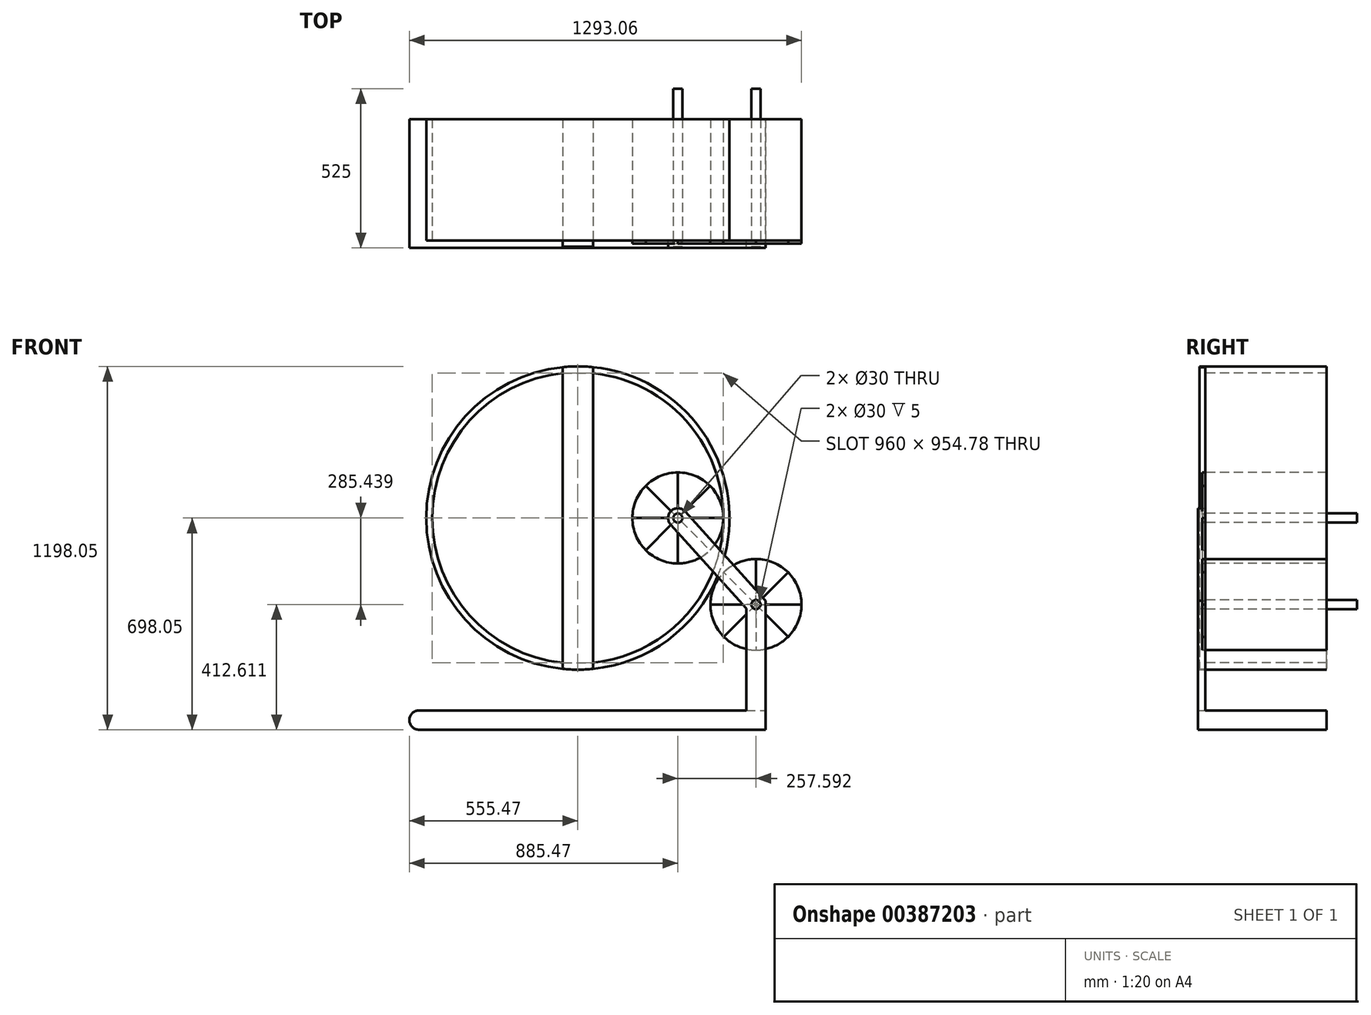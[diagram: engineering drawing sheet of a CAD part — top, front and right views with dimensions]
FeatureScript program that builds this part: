
annotation { "Feature Type Name" : "Feature", "Feature Type Description" : "" }
export const myFeature = defineFeature(function(context is Context, id is Id, definition is map)
    precondition{}
    {
        {
            var Q0;
            Q0=qCreatedBy(makeId("Front.planeOp"),FACE);
            var sketch = newSketch(context, id + "F0", { "sketchPlane" : qUnion([Q0])});
            skCircle(sketch, "E0", {"center": v(0, 0) * mm, "radius": 500 * mm});
            skArc(sketch, "E1", {"start": v(50, -477.39) * mm, "mid": v(480, 0) * mm, "end": v(50, 477.39) * mm});
            skCircle(sketch, "E2", {"center": v(330, 0) * mm, "radius": 150 * mm});
            skCircle(sketch, "E3", {"center": v(587.6, -285.44) * mm, "radius": 150 * mm});
            skLineSegment(sketch, "E4", {"start": v(330, 0) * mm, "end": v(587.6, -285.44) * mm});
            skLineSegment(sketch, "E5", {"start": v(587.6, -666.05) * mm, "end": v(-523.47, -666.05) * mm});
            skLineSegment(sketch, "E6", {"start": v(587.6, -666.05) * mm, "end": v(587.6, -285.44) * mm});
            skLineSegment(sketch, "E7.0", {"start": v(555.6, -634.05) * mm, "end": v(-523.47, -634.05) * mm});
            skLineSegment(sketch, "E7.1", {"start": v(555.6, -634.05) * mm, "end": v(555.6, -297.74) * mm});
            skLineSegment(sketch, "E7.2", {"start": v(306.24, -21.44) * mm, "end": v(555.6, -297.74) * mm});
            skLineSegment(sketch, "E8.0", {"start": v(619.6, -698.05) * mm, "end": v(-523.47, -698.05) * mm});
            skLineSegment(sketch, "E8.1", {"start": v(619.6, -698.05) * mm, "end": v(619.6, -273.13) * mm});
            skLineSegment(sketch, "E8.2", {"start": v(353.76, 21.44) * mm, "end": v(619.6, -273.13) * mm});
            skArc(sketch, "E9", {"start": v(-523.47, -634.05) * mm, "mid": v(-555.47, -666.05) * mm, "end": v(-523.47, -698.05) * mm});
            skArc(sketch, "E10", {"start": v(353.76, 21.44) * mm, "mid": v(308.56, 23.76) * mm, "end": v(306.24, -21.44) * mm});
            skCircle(sketch, "E11", {"center": v(330, 0) * mm, "radius": 15 * mm});
            skCircle(sketch, "E12", {"center": v(587.6, -285.44) * mm, "radius": 15 * mm});
            skLineSegment(sketch, "E13.0", {"start": v(50, 0) * mm, "end": v(50, 477.39) * mm});
            skLineSegment(sketch, "E13.1", {"start": v(50, 0) * mm, "end": v(50, -477.39) * mm});
            skLineSegment(sketch, "E14.0", {"start": v(-50, 0) * mm, "end": v(-50, 477.39) * mm});
            skLineSegment(sketch, "E14.1", {"start": v(-50, 0) * mm, "end": v(-50, -477.39) * mm});
            skArc(sketch, "E15.trimOffspring", {"start": v(-50, 477.39) * mm, "mid": v(-480, 0) * mm, "end": v(-50, -477.39) * mm});
            skCircle(sketch, "E16.cCircle", {"center": v(587.6, -285.44) * mm, "radius": 24.02 * mm, "construction": true});
            skLineSegment(sketch, "E16.0", {"start": v(613.98, -293.98) * mm, "end": v(593.39, -312.56) * mm});
            skLineSegment(sketch, "E16.1", {"start": v(593.39, -312.56) * mm, "end": v(567, -304.02) * mm});
            skLineSegment(sketch, "E16.2", {"start": v(567, -304.02) * mm, "end": v(561.2, -276.9) * mm});
            skLineSegment(sketch, "E16.3", {"start": v(561.2, -276.9) * mm, "end": v(581.8, -258.32) * mm});
            skLineSegment(sketch, "E16.4", {"start": v(581.8, -258.32) * mm, "end": v(608.18, -266.86) * mm});
            skLineSegment(sketch, "E16.5", {"start": v(608.18, -266.86) * mm, "end": v(613.98, -293.98) * mm});
            skPoint(sketch, "E16.0.midPoint", {"position": v(603.68, -303.27) * mm});
            skCircle(sketch, "E17.cCircle", {"center": v(330, 0) * mm, "radius": 22.44 * mm, "construction": true});
            skLineSegment(sketch, "E17.0", {"start": v(350.26, -16.15) * mm, "end": v(326.14, -25.63) * mm});
            skLineSegment(sketch, "E17.1", {"start": v(326.14, -25.63) * mm, "end": v(305.88, -9.47) * mm});
            skLineSegment(sketch, "E17.2", {"start": v(305.88, -9.47) * mm, "end": v(309.74, 16.15) * mm});
            skLineSegment(sketch, "E17.3", {"start": v(309.74, 16.15) * mm, "end": v(333.86, 25.63) * mm});
            skLineSegment(sketch, "E17.4", {"start": v(333.86, 25.63) * mm, "end": v(354.12, 9.47) * mm});
            skLineSegment(sketch, "E17.5", {"start": v(354.12, 9.47) * mm, "end": v(350.26, -16.15) * mm});
            skPoint(sketch, "E17.0.midPoint", {"position": v(338.2, -20.9) * mm});
            skLineSegment(sketch, "E18", {"start": v(555.6, -634.05) * mm, "end": v(619.6, -634.05) * mm});
            skLineSegment(sketch, "E19", {"start": v(-50, 477.39) * mm, "end": v(-50, 497.5) * mm});
            skLineSegment(sketch, "E20", {"start": v(50, 477.39) * mm, "end": v(50, 497.5) * mm});
            skLineSegment(sketch, "E21", {"start": v(-50, 477.39) * mm, "end": v(50, 477.39) * mm});
            skLineSegment(sketch, "E22", {"start": v(-50, -477.39) * mm, "end": v(-50, -497.5) * mm});
            skLineSegment(sketch, "E23", {"start": v(-50, -477.39) * mm, "end": v(50, -477.39) * mm});
            skLineSegment(sketch, "E24", {"start": v(50, -477.39) * mm, "end": v(50, -497.5) * mm});
            skSolve(sketch);
        }
        {
            var Q0;
            {var subQ1=sQuery(id+"F0.wireOp",EDGE,"E7.0");Q0=makeQuery(id+"F0.imprint","IMPRINT",FACE,{"disambiguationData":[TD([[makeQuery(id+"F0.imprint","IMPRINT",EDGE,{"derivedFrom":subQ1}),1.0]])]});}
            var Q1;
            {var subQ10=sQuery(id+"F0.wireOp",EDGE,"E16.2");Q1=makeQuery(id+"F0.imprint","IMPRINT",FACE,{"disambiguationData":[TD([[makeQuery(id+"F0.imprint","IMPRINT",EDGE,{"derivedFrom":subQ10}),1.0]])]});}
            var Q2;
            {var subQ8=sQuery(id+"F0.wireOp",EDGE,"E16.0");Q2=makeQuery(id+"F0.imprint","IMPRINT",FACE,{"disambiguationData":[TD([[makeQuery(id+"F0.imprint","IMPRINT",EDGE,{"derivedFrom":subQ8}),1.0]])]});}
            var Q3;
            {var subQ0=sQuery(id+"F0.wireOp",EDGE,"E7.2");var subQ1=sQuery(id+"F0.wireOp",EDGE,"E0");var subQ2=makeQuery(id+"F0.imprint","INTERSECT",VERTEX,{"derivedFrom":[subQ1,subQ0]});Q3=makeQuery(id+"F0.imprint","IMPRINT",FACE,{"disambiguationData":[TD([[makeQuery(id+"F0.imprint","IMPRINT",EDGE,{"disambiguationData":[TD([[subQ2,-1.0]])],"derivedFrom":subQ1}),-1.0]])]});}
            var Q4;
            {var subQ0=sQuery(id+"F0.wireOp",EDGE,"E7.2");var subQ1=sQuery(id+"F0.wireOp",EDGE,"E0");var subQ2=makeQuery(id+"F0.imprint","INTERSECT",VERTEX,{"derivedFrom":[subQ1,subQ0]});Q4=makeQuery(id+"F0.imprint","IMPRINT",FACE,{"disambiguationData":[TD([[makeQuery(id+"F0.imprint","IMPRINT",EDGE,{"disambiguationData":[TD([[subQ2,-1.0]])],"derivedFrom":subQ1}),1.0]])]});}
            var Q5;
            {var subQ0=sQuery(id+"F0.wireOp",EDGE,"E7.2");var subQ1=sQuery(id+"F0.wireOp",EDGE,"E1");var subQ2=makeQuery(id+"F0.imprint","INTERSECT",VERTEX,{"derivedFrom":[subQ1,subQ0]});Q5=makeQuery(id+"F0.imprint","IMPRINT",FACE,{"disambiguationData":[TD([[makeQuery(id+"F0.imprint","IMPRINT",EDGE,{"disambiguationData":[TD([[subQ2,-1.0]])],"derivedFrom":subQ1}),1.0]])]});}
            var Q6;
            {var subQ0=sQuery(id+"F0.wireOp",EDGE,"E4");var subQ1=sQuery(id+"F0.wireOp",EDGE,"E1");var subQ2=makeQuery(id+"F0.imprint","INTERSECT",VERTEX,{"derivedFrom":[subQ1,subQ0]});Q6=makeQuery(id+"F0.imprint","IMPRINT",FACE,{"disambiguationData":[TD([[makeQuery(id+"F0.imprint","IMPRINT",EDGE,{"disambiguationData":[TD([[subQ2,-1.0]])],"derivedFrom":subQ1}),1.0]])]});}
            var Q7;
            {var subQ4=sQuery(id+"F0.wireOp",EDGE,"E10");Q7=makeQuery(id+"F0.imprint","IMPRINT",FACE,{"disambiguationData":[TD([[makeQuery(id+"F0.imprint","IMPRINT",EDGE,{"derivedFrom":subQ4}),1.0]])]});}
            var Q8;
            {var subQ0=sQuery(id+"F0.wireOp",EDGE,"E8.2");var subQ1=sQuery(id+"F0.wireOp",EDGE,"E0");var subQ2=makeQuery(id+"F0.imprint","INTERSECT",VERTEX,{"derivedFrom":[subQ1,subQ0]});Q8=makeQuery(id+"F0.imprint","IMPRINT",FACE,{"disambiguationData":[TD([[makeQuery(id+"F0.imprint","IMPRINT",EDGE,{"disambiguationData":[TD([[subQ2,1.0]])],"derivedFrom":subQ1}),1.0]])]});}
            var Q9;
            {var subQ0=sQuery(id+"F0.wireOp",EDGE,"E8.2");var subQ1=sQuery(id+"F0.wireOp",EDGE,"E0");var subQ2=makeQuery(id+"F0.imprint","INTERSECT",VERTEX,{"derivedFrom":[subQ1,subQ0]});Q9=makeQuery(id+"F0.imprint","IMPRINT",FACE,{"disambiguationData":[TD([[makeQuery(id+"F0.imprint","IMPRINT",EDGE,{"disambiguationData":[TD([[subQ2,1.0]])],"derivedFrom":subQ1}),-1.0]])]});}
            var Q10;
            {var subQ6=sQuery(id+"F0.wireOp",EDGE,"E16.2");Q10=makeQuery(id+"F0.imprint","IMPRINT",FACE,{"disambiguationData":[TD([[makeQuery(id+"F0.imprint","IMPRINT",EDGE,{"derivedFrom":subQ6}),-1.0]])]});}
            var Q11;
            {var subQ0=sQuery(id+"F0.wireOp",EDGE,"E16.0");Q11=makeQuery(id+"F0.imprint","IMPRINT",FACE,{"disambiguationData":[TD([[makeQuery(id+"F0.imprint","IMPRINT",EDGE,{"derivedFrom":subQ0}),-1.0]])]});}
            var Q12;
            Q12=makeQuery(id+"F0.imprint","IMPRINT",FACE,{"disambiguationData":[TD([[makeQuery(id+"F0.imprint","IMPRINT",EDGE,{"derivedFrom":sQuery(id+"F0.wireOp",EDGE,"E11")}),-1.0]])]});
            var Q13;
            {var subQ0=sQuery(id+"F0.wireOp",EDGE,"E7.1");var subQ1=sQuery(id+"F0.wireOp",EDGE,"E3");var subQ2=makeQuery(id+"F0.imprint","INTERSECT",VERTEX,{"derivedFrom":[subQ1,subQ0]});Q13=makeQuery(id+"F0.imprint","IMPRINT",FACE,{"disambiguationData":[TD([[makeQuery(id+"F0.imprint","IMPRINT",EDGE,{"disambiguationData":[TD([[subQ2,-1.0]])],"derivedFrom":subQ1}),-1.0]])]});}
            var Q14;
            {var subQ0=sQuery(id+"F0.wireOp",EDGE,"E8.1");var subQ1=sQuery(id+"F0.wireOp",EDGE,"E3");var subQ2=makeQuery(id+"F0.imprint","INTERSECT",VERTEX,{"derivedFrom":[subQ1,subQ0]});Q14=makeQuery(id+"F0.imprint","IMPRINT",FACE,{"disambiguationData":[TD([[makeQuery(id+"F0.imprint","IMPRINT",EDGE,{"disambiguationData":[TD([[subQ2,1.0]])],"derivedFrom":subQ1}),-1.0]])]});}
            extrude(context, id + "F1", {"entities" : qUnion([Q0, Q1, Q2, Q3, Q4, Q5, Q6, Q7, Q8, Q9, Q10, Q11, Q12, Q13, Q14]), "depth" : 25 * mm});
        }
        {
            var Q0;
            {var subQ4=sQuery(id+"F0.wireOp",EDGE,"E7.0");Q0=makeQuery(id+"F0.imprint","IMPRINT",FACE,{"disambiguationData":[TD([[makeQuery(id+"F0.imprint","IMPRINT",EDGE,{"derivedFrom":subQ4}),1.0]])]});}
            extrude(context, id + "F2", {"entities" : qUnion([Q0]), "operationType" : NewBodyOperationType.ADD, "oppositeDirection" : true, "depth" : 400 * mm});
        }
        {
            var Q0;
            Q0=makeQuery(id+"F0.imprint","IMPRINT",FACE,{"disambiguationData":[TD([[makeQuery(id+"F0.imprint","IMPRINT",EDGE,{"derivedFrom":sQuery(id+"F0.wireOp",EDGE,"E11")}),-1.0]])]});
            var Q1;
            Q1=makeQuery(id+"F0.imprint","IMPRINT",FACE,{"disambiguationData":[TD([[makeQuery(id+"F0.imprint","IMPRINT",EDGE,{"derivedFrom":sQuery(id+"F0.wireOp",EDGE,"E11")}),1.0]])]});
            var Q2;
            {var subQ8=sQuery(id+"F0.wireOp",EDGE,"E16.2");Q2=makeQuery(id+"F0.imprint","IMPRINT",FACE,{"disambiguationData":[TD([[makeQuery(id+"F0.imprint","IMPRINT",EDGE,{"derivedFrom":subQ8}),-1.0]])]});}
            var Q3;
            {var subQ0=sQuery(id+"F0.wireOp",EDGE,"E16.0");Q3=makeQuery(id+"F0.imprint","IMPRINT",FACE,{"disambiguationData":[TD([[makeQuery(id+"F0.imprint","IMPRINT",EDGE,{"derivedFrom":subQ0}),-1.0]])]});}
            var Q4;
            {var subQ0=sQuery(id+"F0.wireOp",EDGE,"E6");var subQ1=sQuery(id+"F0.wireOp",EDGE,"E4");var subQ2=makeQuery(id+"F0.imprint","INTERSECT",VERTEX,{"derivedFrom":[subQ1,subQ0]});Q4=makeQuery(id+"F0.imprint","IMPRINT",FACE,{"disambiguationData":[TD([[makeQuery(id+"F0.imprint","IMPRINT",EDGE,{"disambiguationData":[TD([[subQ2,1.0]])],"derivedFrom":subQ1}),1.0]])]});}
            var Q5;
            {var subQ0=sQuery(id+"F0.wireOp",EDGE,"E6");var subQ1=sQuery(id+"F0.wireOp",EDGE,"E4");var subQ2=makeQuery(id+"F0.imprint","INTERSECT",VERTEX,{"derivedFrom":[subQ1,subQ0]});Q5=makeQuery(id+"F0.imprint","IMPRINT",FACE,{"disambiguationData":[TD([[makeQuery(id+"F0.imprint","IMPRINT",EDGE,{"disambiguationData":[TD([[subQ2,1.0]])],"derivedFrom":subQ1}),-1.0]])]});}
            extrude(context, id + "F3", {"entities" : qUnion([Q0, Q1, Q2, Q3, Q4, Q5]), "depth" : 20 * mm});
        }
        {
            var Q0;
            Q0=makeQuery(id+"F0.imprint","IMPRINT",FACE,{"disambiguationData":[TD([[makeQuery(id+"F0.imprint","IMPRINT",EDGE,{"derivedFrom":sQuery(id+"F0.wireOp",EDGE,"E11")}),1.0]])]});
            extrude(context, id + "F4", {"entities" : qUnion([Q0]), "operationType" : NewBodyOperationType.ADD, "oppositeDirection" : true, "depth" : 500 * mm});
        }
        {
            var Q0;
            {var subQ0=sQuery(id+"F0.wireOp",EDGE,"E6");var subQ1=sQuery(id+"F0.wireOp",EDGE,"E4");var subQ2=makeQuery(id+"F0.imprint","INTERSECT",VERTEX,{"derivedFrom":[subQ1,subQ0]});Q0=makeQuery(id+"F0.imprint","IMPRINT",FACE,{"disambiguationData":[TD([[makeQuery(id+"F0.imprint","IMPRINT",EDGE,{"disambiguationData":[TD([[subQ2,1.0]])],"derivedFrom":subQ1}),1.0]])]});}
            var Q1;
            {var subQ0=sQuery(id+"F0.wireOp",EDGE,"E6");var subQ1=sQuery(id+"F0.wireOp",EDGE,"E4");var subQ2=makeQuery(id+"F0.imprint","INTERSECT",VERTEX,{"derivedFrom":[subQ1,subQ0]});Q1=makeQuery(id+"F0.imprint","IMPRINT",FACE,{"disambiguationData":[TD([[makeQuery(id+"F0.imprint","IMPRINT",EDGE,{"disambiguationData":[TD([[subQ2,1.0]])],"derivedFrom":subQ1}),-1.0]])]});}
            extrude(context, id + "F5", {"entities" : qUnion([Q0, Q1]), "operationType" : NewBodyOperationType.ADD, "oppositeDirection" : true, "depth" : 500 * mm});
        }
        {
            var Q0;
            {var subQ0=sQuery(id+"F0.wireOp",EDGE,"E8.2");var subQ1=sQuery(id+"F0.wireOp",EDGE,"E3");var subQ2=makeQuery(id+"F0.imprint","INTERSECT",VERTEX,{"derivedFrom":[subQ1,subQ0]});Q0=makeQuery(id+"F0.imprint","IMPRINT",FACE,{"disambiguationData":[TD([[makeQuery(id+"F0.imprint","IMPRINT",EDGE,{"disambiguationData":[TD([[subQ2,1.0]])],"derivedFrom":subQ1}),1.0]])]});}
            var Q1;
            {var subQ0=sQuery(id+"F0.wireOp",EDGE,"E16.0");Q1=makeQuery(id+"F0.imprint","IMPRINT",FACE,{"disambiguationData":[TD([[makeQuery(id+"F0.imprint","IMPRINT",EDGE,{"derivedFrom":subQ0}),1.0]])]});}
            var Q2;
            {var subQ9=sQuery(id+"F0.wireOp",EDGE,"E16.2");Q2=makeQuery(id+"F0.imprint","IMPRINT",FACE,{"disambiguationData":[TD([[makeQuery(id+"F0.imprint","IMPRINT",EDGE,{"derivedFrom":subQ9}),1.0]])]});}
            var Q3;
            {var subQ0=sQuery(id+"F0.wireOp",EDGE,"E7.2");var subQ1=sQuery(id+"F0.wireOp",EDGE,"E3");var subQ2=makeQuery(id+"F0.imprint","INTERSECT",VERTEX,{"derivedFrom":[subQ1,subQ0]});Q3=makeQuery(id+"F0.imprint","IMPRINT",FACE,{"disambiguationData":[TD([[makeQuery(id+"F0.imprint","IMPRINT",EDGE,{"disambiguationData":[TD([[subQ2,-1.0]])],"derivedFrom":subQ1}),1.0]])]});}
            var Q4;
            {var subQ8=sQuery(id+"F0.wireOp",EDGE,"E16.2");Q4=makeQuery(id+"F0.imprint","IMPRINT",FACE,{"disambiguationData":[TD([[makeQuery(id+"F0.imprint","IMPRINT",EDGE,{"derivedFrom":subQ8}),-1.0]])]});}
            var Q5;
            {var subQ0=sQuery(id+"F0.wireOp",EDGE,"E16.0");Q5=makeQuery(id+"F0.imprint","IMPRINT",FACE,{"disambiguationData":[TD([[makeQuery(id+"F0.imprint","IMPRINT",EDGE,{"derivedFrom":subQ0}),-1.0]])]});}
            var Q6;
            {var subQ0=sQuery(id+"F0.wireOp",EDGE,"E10");Q6=makeQuery(id+"F0.imprint","IMPRINT",FACE,{"disambiguationData":[TD([[makeQuery(id+"F0.imprint","IMPRINT",EDGE,{"derivedFrom":subQ0}),-1.0]])]});}
            var Q7;
            {var subQ3=sQuery(id+"F0.wireOp",EDGE,"E10");Q7=makeQuery(id+"F0.imprint","IMPRINT",FACE,{"disambiguationData":[TD([[makeQuery(id+"F0.imprint","IMPRINT",EDGE,{"derivedFrom":subQ3}),1.0]])]});}
            var Q8;
            Q8=makeQuery(id+"F0.imprint","IMPRINT",FACE,{"disambiguationData":[TD([[makeQuery(id+"F0.imprint","IMPRINT",EDGE,{"derivedFrom":sQuery(id+"F0.wireOp",EDGE,"E11")}),-1.0]])]});
            extrude(context, id + "F6", {"entities" : qUnion([Q0, Q1, Q2, Q3, Q4, Q5, Q6, Q7, Q8]), "oppositeDirection" : true, "depth" : 400 * mm});
        }
        {
            var Q0;
            {var subQ6=sQuery(id+"F0.wireOp",EDGE,"E20");Q0=makeQuery(id+"F0.imprint","IMPRINT",FACE,{"disambiguationData":[TD([[makeQuery(id+"F0.imprint","IMPRINT",EDGE,{"derivedFrom":subQ6}),-1.0]])]});}
            var Q1;
            {var subQ0=sQuery(id+"F0.wireOp",EDGE,"E8.2");var subQ1=sQuery(id+"F0.wireOp",EDGE,"E0");var subQ2=makeQuery(id+"F0.imprint","INTERSECT",VERTEX,{"derivedFrom":[subQ1,subQ0]});Q1=makeQuery(id+"F0.imprint","IMPRINT",FACE,{"disambiguationData":[TD([[makeQuery(id+"F0.imprint","IMPRINT",EDGE,{"disambiguationData":[TD([[subQ2,1.0]])],"derivedFrom":subQ1}),1.0]])]});}
            var Q2;
            {var subQ0=sQuery(id+"F0.wireOp",EDGE,"E7.2");var subQ1=sQuery(id+"F0.wireOp",EDGE,"E0");var subQ2=makeQuery(id+"F0.imprint","INTERSECT",VERTEX,{"derivedFrom":[subQ1,subQ0]});Q2=makeQuery(id+"F0.imprint","IMPRINT",FACE,{"disambiguationData":[TD([[makeQuery(id+"F0.imprint","IMPRINT",EDGE,{"disambiguationData":[TD([[subQ2,-1.0]])],"derivedFrom":subQ1}),1.0]])]});}
            var Q3;
            {var subQ0=sQuery(id+"F0.wireOp",EDGE,"E24");Q3=makeQuery(id+"F0.imprint","IMPRINT",FACE,{"disambiguationData":[TD([[makeQuery(id+"F0.imprint","IMPRINT",EDGE,{"derivedFrom":subQ0}),1.0]])]});}
            var Q4;
            {var subQ0=sQuery(id+"F0.wireOp",EDGE,"E19");Q4=makeQuery(id+"F0.imprint","IMPRINT",FACE,{"disambiguationData":[TD([[makeQuery(id+"F0.imprint","IMPRINT",EDGE,{"derivedFrom":subQ0}),-1.0]])]});}
            var Q5;
            Q5=makeQuery(id+"F0.imprint","IMPRINT",FACE,{"disambiguationData":[TD([[makeQuery(id+"F0.imprint","IMPRINT",EDGE,{"derivedFrom":sQuery(id+"F0.wireOp",EDGE,"E15.trimOffspring")}),-1.0]])]});
            var Q6;
            {var subQ0=sQuery(id+"F0.wireOp",EDGE,"E22");Q6=makeQuery(id+"F0.imprint","IMPRINT",FACE,{"disambiguationData":[TD([[makeQuery(id+"F0.imprint","IMPRINT",EDGE,{"derivedFrom":subQ0}),1.0]])]});}
            extrude(context, id + "F7", {"entities" : qUnion([Q0, Q1, Q2, Q3, Q4, Q5, Q6]), "oppositeDirection" : true, "depth" : 400 * mm});
        }
        {
            var Q0;
            Q0=makeQuery(id+"F0.imprint","IMPRINT",FACE,{"disambiguationData":[TD([[makeQuery(id+"F0.imprint","IMPRINT",EDGE,{"derivedFrom":sQuery(id+"F0.wireOp",EDGE,"E13.0")}),1.0]])]});
            var Q1;
            {var subQ0=sQuery(id+"F0.wireOp",EDGE,"E19");Q1=makeQuery(id+"F0.imprint","IMPRINT",FACE,{"disambiguationData":[TD([[makeQuery(id+"F0.imprint","IMPRINT",EDGE,{"derivedFrom":subQ0}),-1.0]])]});}
            var Q2;
            {var subQ0=sQuery(id+"F0.wireOp",EDGE,"E22");Q2=makeQuery(id+"F0.imprint","IMPRINT",FACE,{"disambiguationData":[TD([[makeQuery(id+"F0.imprint","IMPRINT",EDGE,{"derivedFrom":subQ0}),1.0]])]});}
            extrude(context, id + "F8", {"entities" : qUnion([Q0, Q1, Q2]), "depth" : 20 * mm});
        }
        {
            var Q0;
            Q0=makeQuery(id+"F6.opExtrude","CAP_FACE",FACE,{"disambiguationData":[OSD([sQuery(id+"F0.wireOp",EDGE,"E2"),sQuery(id+"F0.wireOp",EDGE,"E11")])],"isStart":true});
            var sketch = newSketch(context, id + "F9", { "sketchPlane" : qUnion([Q0])});
            skCircle(sketch, "E25.0.0", {"center": v(330, 0) * mm, "radius": 150 * mm});
            skCircle(sketch, "E26.0.0", {"center": v(587.6, -285.44) * mm, "radius": 150 * mm});
            skLineSegment(sketch, "E27", {"start": v(330, 0) * mm, "end": v(330, -150) * mm});
            skLineSegment(sketch, "E28", {"start": v(587.6, -285.44) * mm, "end": v(587.6, -435.44) * mm});
            skLineSegment(sketch, "E29.1.0", {"start": v(330, 0) * mm, "end": v(223.93, -106.07) * mm});
            skLineSegment(sketch, "E29.2.0", {"start": v(330, 0) * mm, "end": v(180, 0) * mm});
            skLineSegment(sketch, "E29.3.0", {"start": v(330, 0) * mm, "end": v(223.93, 106.07) * mm});
            skLineSegment(sketch, "E29.4.0", {"start": v(330, 0) * mm, "end": v(330, 150) * mm});
            skLineSegment(sketch, "E29.5.0", {"start": v(330, 0) * mm, "end": v(436.07, 106.07) * mm});
            skLineSegment(sketch, "E29.6.0", {"start": v(330, 0) * mm, "end": v(480, 0) * mm});
            skLineSegment(sketch, "E29.7.0", {"start": v(330, 0) * mm, "end": v(436.07, -106.07) * mm});
            skLineSegment(sketch, "E29.anchor1", {"start": v(330, 0) * mm, "end": v(330, -150) * mm, "construction": true});
            skLineSegment(sketch, "E29.anchor2", {"start": v(330, 0) * mm, "end": v(436.07, -106.07) * mm, "construction": true});
            skLineSegment(sketch, "E30.1.0", {"start": v(587.6, -285.44) * mm, "end": v(693.66, -391.5) * mm});
            skLineSegment(sketch, "E30.2.0", {"start": v(587.6, -285.44) * mm, "end": v(737.6, -285.44) * mm});
            skLineSegment(sketch, "E30.3.0", {"start": v(587.6, -285.44) * mm, "end": v(693.66, -179.37) * mm});
            skLineSegment(sketch, "E30.4.0", {"start": v(587.6, -285.44) * mm, "end": v(587.6, -135.44) * mm});
            skLineSegment(sketch, "E30.5.0", {"start": v(587.6, -285.44) * mm, "end": v(481.53, -179.37) * mm});
            skLineSegment(sketch, "E30.6.0", {"start": v(587.6, -285.44) * mm, "end": v(437.6, -285.44) * mm});
            skLineSegment(sketch, "E30.7.0", {"start": v(587.6, -285.44) * mm, "end": v(481.53, -391.5) * mm});
            skSolve(sketch);
        }
        {
            var Q0;
            {var subQ0=sQuery(id+"F9.wireOp",EDGE,"E27");var subQ1=sQuery(id+"F9.wireOp",EDGE,"E25.0.0");var subQ2=makeQuery(id+"F9.imprint","INTERSECT",VERTEX,{"derivedFrom":[subQ1,subQ0]});Q0=makeQuery(id+"F9.imprint","IMPRINT",FACE,{"disambiguationData":[TD([[makeQuery(id+"F9.imprint","IMPRINT",EDGE,{"disambiguationData":[TD([[subQ2,1.0]])],"derivedFrom":subQ1}),1.0]])]});}
            var Q1;
            {var subQ0=sQuery(id+"F9.wireOp",EDGE,"E29.2.0");var subQ1=sQuery(id+"F9.wireOp",EDGE,"E25.0.0");var subQ2=makeQuery(id+"F9.imprint","INTERSECT",VERTEX,{"derivedFrom":[subQ1,subQ0]});Q1=makeQuery(id+"F9.imprint","IMPRINT",FACE,{"disambiguationData":[TD([[makeQuery(id+"F9.imprint","IMPRINT",EDGE,{"disambiguationData":[TD([[subQ2,1.0]])],"derivedFrom":subQ1}),1.0]])]});}
            var Q2;
            {var subQ0=sQuery(id+"F9.wireOp",EDGE,"E29.4.0");var subQ1=sQuery(id+"F9.wireOp",EDGE,"E25.0.0");var subQ2=makeQuery(id+"F9.imprint","INTERSECT",VERTEX,{"derivedFrom":[subQ1,subQ0]});Q2=makeQuery(id+"F9.imprint","IMPRINT",FACE,{"disambiguationData":[TD([[makeQuery(id+"F9.imprint","IMPRINT",EDGE,{"disambiguationData":[TD([[subQ2,1.0]])],"derivedFrom":subQ1}),1.0]])]});}
            var Q3;
            {var subQ0=sQuery(id+"F9.wireOp",EDGE,"E29.6.0");var subQ1=sQuery(id+"F9.wireOp",EDGE,"E25.0.0");var subQ2=makeQuery(id+"F9.imprint","INTERSECT",VERTEX,{"derivedFrom":[subQ1,subQ0]});Q3=makeQuery(id+"F9.imprint","IMPRINT",FACE,{"disambiguationData":[TD([[makeQuery(id+"F9.imprint","IMPRINT",EDGE,{"disambiguationData":[TD([[subQ2,1.0]])],"derivedFrom":subQ1}),1.0]])]});}
            var Q4;
            {var subQ0=sQuery(id+"F9.wireOp",EDGE,"E30.6.0");Q4=makeQuery(id+"F9.imprint","IMPRINT",FACE,{"disambiguationData":[TD([[makeQuery(id+"F9.imprint","IMPRINT",EDGE,{"derivedFrom":subQ0}),1.0]])]});}
            var Q5;
            {var subQ0=sQuery(id+"F9.wireOp",EDGE,"E30.4.0");Q5=makeQuery(id+"F9.imprint","IMPRINT",FACE,{"disambiguationData":[TD([[makeQuery(id+"F9.imprint","IMPRINT",EDGE,{"derivedFrom":subQ0}),1.0]])]});}
            var Q6;
            {var subQ0=sQuery(id+"F9.wireOp",EDGE,"E30.2.0");Q6=makeQuery(id+"F9.imprint","IMPRINT",FACE,{"disambiguationData":[TD([[makeQuery(id+"F9.imprint","IMPRINT",EDGE,{"derivedFrom":subQ0}),1.0]])]});}
            var Q7;
            {var subQ0=sQuery(id+"F9.wireOp",EDGE,"E28");Q7=makeQuery(id+"F9.imprint","IMPRINT",FACE,{"disambiguationData":[TD([[makeQuery(id+"F9.imprint","IMPRINT",EDGE,{"derivedFrom":subQ0}),1.0]])]});}
            extrude(context, id + "F10", {"entities" : qUnion([Q0, Q1, Q2, Q3, Q4, Q5, Q6, Q7]), "depth" : 10 * mm});
        }
    });
